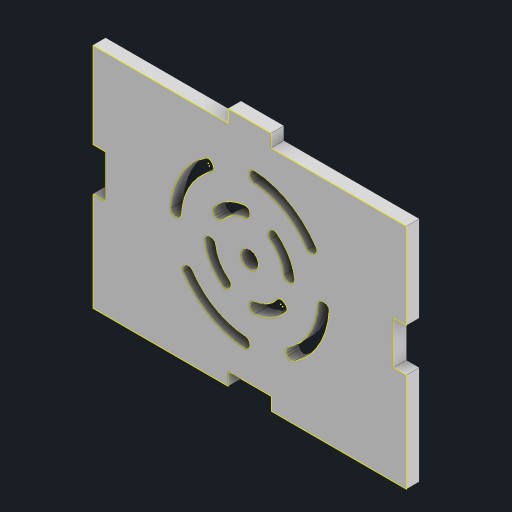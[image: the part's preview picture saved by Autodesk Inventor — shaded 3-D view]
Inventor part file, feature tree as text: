
AUTODESK INVENTOR PART (.ipt)
format: ipt  version: 2023 (Build 270158000, 158)  size: 276,992 bytes
history: native  units: mm
features: extrude x5, sketch x5, fillet x1, pattern_circular x1, projected_geometry x1
ambient origin geometry x8: Origin, YZ Plane, XZ Plane, XY Plane, X Axis, Y Axis, Z Axis, Center Point
bodies: Solid1 (feature_tree)
feature tree (13):
  extrude  "Extrusion1"  Depth=56.0mm
  sketch  "Sketch2"  dims[d2=3.0mm d3=0.0mm d4=3.0mm d5=10.0mm]
  extrude  "Extrusion3"  Depth=3.0mm
  fillet  "Fillet1"  Radius=10.0mm
  pattern_circular  "Circular Pattern1"  [2 undecoded]
  extrude  "Extrusion6"  Depth=3.0mm
  sketch  "Sketch6"  dims[d7=16.0mm]
  extrude  "Extrusion7"  TaperAngle=60.0deg  [1 undecoded]
  extrude  "Extrusion8"  TaperAngle=60.0deg  [1 undecoded]
  sketch  "Sketch7"  dims[d8=21.0mm d9=32.0mm d10=37.0mm d11=60.0deg d12=60.0deg d15=1.0mm d16=10.0mm d17=0.0mm d18=40.0mm d19=360.0deg d31=10.0mm d32=3.0mm d33=36.5mm d34=10.0mm d35=3.0mm d36=3.0mm d37=10.0mm d38=3.0mm d39=10.0mm d40=0.0mm d41=0.0mm d42=3.0mm d43=0.0mm d44=0.0mm d45=0.0mm]
  sketch  "Sketch1"  dims[d0=73.0mm d1=56.0mm]
  sketch  "Sketch5"  dims[d6=4.0mm]
  projected_geometry  "Project Cut Edges1"
note: 4 required parameter values undecoded (feature->parameter linkage not recoverable at this tier; creation-order binding heuristic only, values carry confidence <= 0.55)
